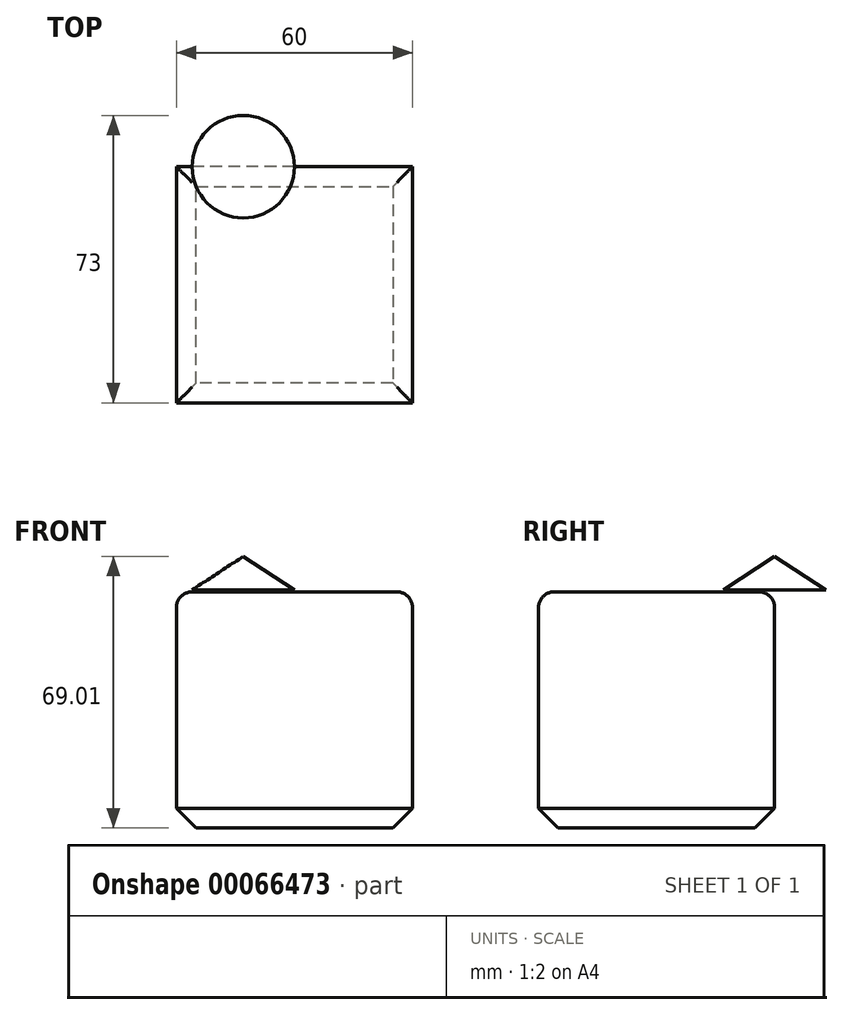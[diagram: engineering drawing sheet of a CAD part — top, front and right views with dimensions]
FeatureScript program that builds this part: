
annotation { "Feature Type Name" : "Feature", "Feature Type Description" : "" }
export const myFeature = defineFeature(function(context is Context, id is Id, definition is map)
    precondition{}
    {
        {
            var Q0;
            Q0=qCreatedBy(makeId("Front.planeOp"),FACE);
            var sketch = newSketch(context, id + "F0", { "sketchPlane" : qUnion([Q0])});
            skLineSegment(sketch, "E0.rect.bottom", {"start": v(30, 30) * mm, "end": v(-30, 30) * mm});
            skLineSegment(sketch, "E0.rect.top", {"start": v(30, -30) * mm, "end": v(-30, -30) * mm});
            skLineSegment(sketch, "E0.rect.left", {"start": v(30, 30) * mm, "end": v(30, -30) * mm});
            skLineSegment(sketch, "E0.rect.right", {"start": v(-30, 30) * mm, "end": v(-30, -30) * mm});
            skPoint(sketch, "E0.rect.middle", {"position": v(0, 0) * mm});
            skSolve(sketch);
        }
        {
            var Q0;
            Q0=makeQuery(id+"F0.imprint","IMPRINT",FACE,{"disambiguationData":[TD([[makeQuery(id+"F0.imprint","IMPRINT",EDGE,{"derivedFrom":sQuery(id+"F0.wireOp",EDGE,"E0.rect.bottom")}),1.0]])]});
            extrude(context, id + "F1", {"entities" : qUnion([Q0]), "depth" : 60 * mm});
        }
        {
            var Q0;
            Q0=makeQuery(id+"F1.opExtrude","CAP_EDGE",EDGE,{"disambiguationData":[OSD([sQuery(id+"F0.wireOp",EDGE,"E0.rect.bottom")])],"isStart":false});
            var Q1;
            Q1=makeQuery(id+"F1.opExtrude","SWEPT_EDGE",EDGE,{"disambiguationData":[OSD([sQuery(id+"F0.wireOp",EDGE,"E0.rect.bottom"),sQuery(id+"F0.wireOp",EDGE,"E0.rect.left")])]});
            var Q2;
            Q2=makeQuery(id+"F1.opExtrude","CAP_EDGE",EDGE,{"disambiguationData":[OSD([sQuery(id+"F0.wireOp",EDGE,"E0.rect.bottom")])],"isStart":true});
            var Q3;
            Q3=makeQuery(id+"F1.opExtrude","SWEPT_EDGE",EDGE,{"disambiguationData":[OSD([sQuery(id+"F0.wireOp",EDGE,"E0.rect.bottom"),sQuery(id+"F0.wireOp",EDGE,"E0.rect.right")])]});
            fillet(context, id + "F2", {"entities" : qUnion([Q0, Q1, Q2, Q3]), "radius" : 4 * mm, "tangentPropagation" : true, "allowEdgeOverflow" : false});
        }
        {
            var Q0;
            Q0=makeQuery(id+"F1.opExtrude","CAP_EDGE",EDGE,{"disambiguationData":[OSD([sQuery(id+"F0.wireOp",EDGE,"E0.rect.top")])],"isStart":false});
            var Q1;
            Q1=makeQuery(id+"F1.opExtrude","SWEPT_EDGE",EDGE,{"disambiguationData":[OSD([sQuery(id+"F0.wireOp",EDGE,"E0.rect.top"),sQuery(id+"F0.wireOp",EDGE,"E0.rect.left")])]});
            var Q2;
            Q2=makeQuery(id+"F1.opExtrude","CAP_EDGE",EDGE,{"disambiguationData":[OSD([sQuery(id+"F0.wireOp",EDGE,"E0.rect.top")])],"isStart":true});
            var Q3;
            Q3=makeQuery(id+"F1.opExtrude","SWEPT_EDGE",EDGE,{"disambiguationData":[OSD([sQuery(id+"F0.wireOp",EDGE,"E0.rect.top"),sQuery(id+"F0.wireOp",EDGE,"E0.rect.right")])]});
            chamfer(context, id + "F3", {"entities" : qUnion([Q0, Q1, Q2, Q3]), "width" : 5 * mm, "tangentPropagation" : true});
        }
        {
            var Q0;
            Q0=qCreatedBy(makeId("Front.planeOp"),FACE);
            var sketch = newSketch(context, id + "F4", { "sketchPlane" : qUnion([Q0])});
            skLineSegment(sketch, "E1", {"start": v(-13, 39) * mm, "end": v(-13, 30.46) * mm});
            skLineSegment(sketch, "E2", {"start": v(-13, 30.46) * mm, "end": v(0, 30.46) * mm});
            skLineSegment(sketch, "E3", {"start": v(-13, 39) * mm, "end": v(0, 30.46) * mm});
            skSolve(sketch);
        }
        {
            var Q0;
            Q0 = qSketchRegion(id + "F4", true);
            var Q1;
            Q1=sQuery(id+"F4.wireOp",EDGE,"E1");
            revolve(context, id + "F5", {"entities" : qUnion([Q0]), "axis" : qUnion([Q1]), "revolveType" : RevolveType.FULL});
        }
    });
